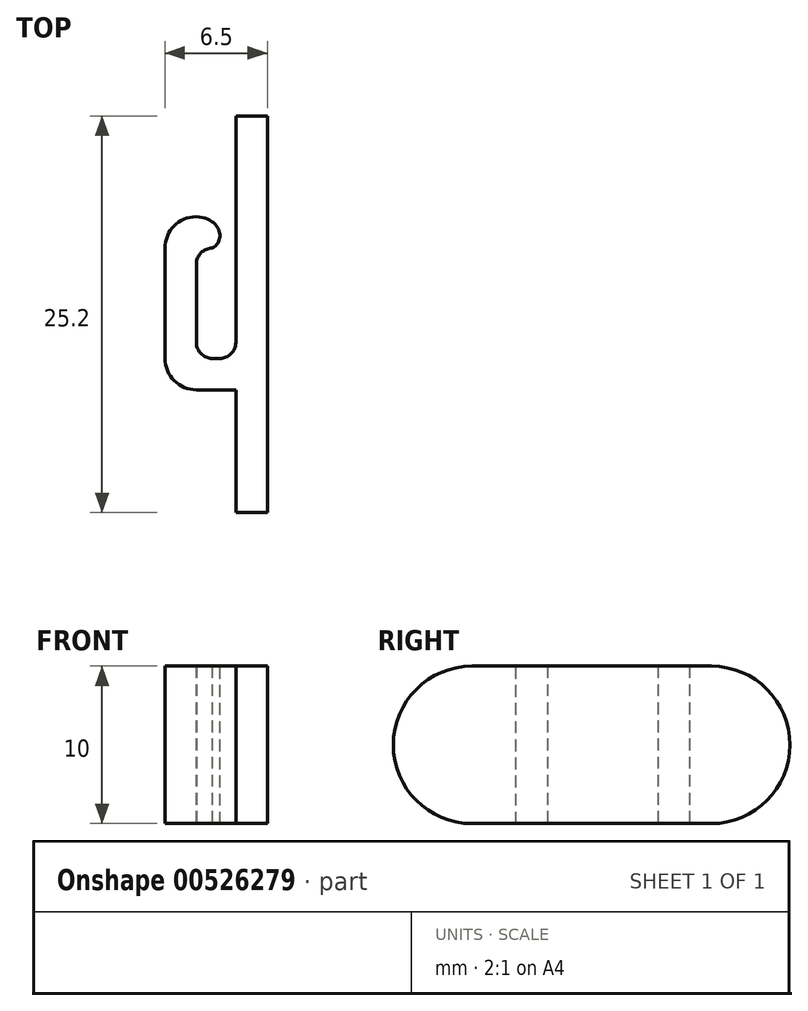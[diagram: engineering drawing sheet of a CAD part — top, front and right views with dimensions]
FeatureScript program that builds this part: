
annotation { "Feature Type Name" : "Feature", "Feature Type Description" : "" }
export const myFeature = defineFeature(function(context is Context, id is Id, definition is map)
    precondition{}
    {
        {
            var Q0;
            Q0=qCreatedBy(makeId("Top.planeOp"),FACE);
            var sketch = newSketch(context, id + "F0", { "sketchPlane" : qUnion([Q0])});
            skPoint(sketch, "E0.middle", {"position": v(0, 0) * mm});
            skLineSegment(sketch, "E1.0", {"start": v(3.25, -5.5) * mm, "end": v(3.25, 3.5) * mm});
            skLineSegment(sketch, "E1.1", {"start": v(3.25, -5.5) * mm, "end": v(-1.25, -5.5) * mm});
            skLineSegment(sketch, "E1.2", {"start": v(-3.25, -3.5) * mm, "end": v(-3.25, 3.5) * mm});
            skPoint(sketch, "E2.visualSharp", {"position": v(-3.25, 5) * mm});
            skArc(sketch, "E2.filletArc", {"start": v(-1.27, 5.5) * mm, "mid": v(-2.67, 4.9) * mm, "end": v(-3.25, 3.5) * mm});
            skPoint(sketch, "E3.visualSharp", {"position": v(-3.25, -5.5) * mm});
            skArc(sketch, "E3.filletArc", {"start": v(-3.25, -3.5) * mm, "mid": v(-2.66, -4.91) * mm, "end": v(-1.25, -5.5) * mm});
            skLineSegment(sketch, "E4.bottom", {"start": v(-0.25, 3.5) * mm, "end": v(0.25, 3.5) * mm, "construction": true});
            skLineSegment(sketch, "E4.top", {"start": v(-0.25, -3.5) * mm, "end": v(0.25, -3.5) * mm});
            skLineSegment(sketch, "E4.left", {"start": v(-1.25, 2.5) * mm, "end": v(-1.25, -2.5) * mm});
            skLineSegment(sketch, "E4.right", {"start": v(1.25, 3.5) * mm, "end": v(1.25, -2.5) * mm});
            skArc(sketch, "E5.filletArc", {"start": v(-0.25, 3.5) * mm, "mid": v(-0.96, 3.2) * mm, "end": v(-1.25, 2.5) * mm});
            skArc(sketch, "E6.filletArc", {"start": v(-1.25, -2.5) * mm, "mid": v(-0.96, -3.2) * mm, "end": v(-0.25, -3.5) * mm});
            skPoint(sketch, "E7.visualSharp", {"position": v(1.25, -3.5) * mm});
            skArc(sketch, "E7.filletArc", {"start": v(0.25, -3.5) * mm, "mid": v(0.96, -3.2) * mm, "end": v(1.25, -2.5) * mm});
            skArc(sketch, "E8", {"start": v(3.25, 3.5) * mm, "mid": v(2.25, 4.5) * mm, "end": v(1.25, 3.5) * mm});
            skFitSpline(sketch, "E9", {"points": [v(-1.27, 5.5) * mm, v(-0.25, 3.5) * mm], "startDerivative": vector(4.8, -0.22) * mm, "endDerivative": vector(-2.68, -1.37) * mm});
            skSolve(sketch);
        }
        {
            var Q0;
            Q0=makeQuery(id+"F0.imprint","IMPRINT",FACE,{"disambiguationData":[TD([[makeQuery(id+"F0.imprint","IMPRINT",EDGE,{"derivedFrom":sQuery(id+"F0.wireOp",EDGE,"E1.0")}),1.0]])]});
            extrude(context, id + "F1", {"entities" : qUnion([Q0]), "depth" : 10 * mm, "offsetDistance" : 25 * mm});
        }
        {
            var Q0;
            Q0=qCreatedBy(makeId("Front.planeOp"),FACE);
            var sketch = newSketch(context, id + "F2", { "sketchPlane" : qUnion([Q0])});
            skLineSegment(sketch, "E10.bottom", {"start": v(3.25, 10) * mm, "end": v(1.25, 10) * mm});
            skLineSegment(sketch, "E10.top", {"start": v(3.25, 0) * mm, "end": v(1.25, 0) * mm});
            skLineSegment(sketch, "E10.left", {"start": v(3.25, 10) * mm, "end": v(3.25, 0) * mm});
            skLineSegment(sketch, "E10.right", {"start": v(1.25, 10) * mm, "end": v(1.25, 0) * mm});
            skSolve(sketch);
        }
        {
            var Q0;
            Q0 = qSketchRegion(id + "F2", true);
            extrude(context, id + "F3", {"entities" : qUnion([Q0]), "operationType" : NewBodyOperationType.ADD, "depth" : 13.3 * mm, "offsetDistance" : 25 * mm, "hasSecondDirection" : true, "secondDirectionOppositeDirection" : true, "secondDirectionDepth" : 11.9 * mm});
        }
        {
            var Q0;
            Q0=makeQuery(id+"F3.opExtrude","CAP_EDGE",EDGE,{"disambiguationData":[OSD([sQuery(id+"F2.wireOp",EDGE,"E10.bottom")])],"isStart":false});
            var Q1;
            Q1=makeQuery(id+"F3.opExtrude","CAP_EDGE",EDGE,{"disambiguationData":[OSD([sQuery(id+"F2.wireOp",EDGE,"E10.bottom")])],"isStart":true});
            var Q2;
            Q2=makeQuery(id+"F3.opExtrude","CAP_EDGE",EDGE,{"disambiguationData":[OSD([sQuery(id+"F2.wireOp",EDGE,"E10.top")])],"isStart":false});
            var Q3;
            Q3=makeQuery(id+"F3.opExtrude","CAP_EDGE",EDGE,{"disambiguationData":[OSD([sQuery(id+"F2.wireOp",EDGE,"E10.top")])],"isStart":true});
            fillet(context, id + "F4", {"entities" : qUnion([Q0, Q1, Q2, Q3]), "radius" : 5 * mm, "tangentPropagation" : true, "allowEdgeOverflow" : false});
        }
    });
